# Revit family: QF_BOURGEAT_Transtherm_chariot_petit_dejeuner_6GN1_1
name_source: partatom
category: Equipement spécialisé
revit_build: Autodesk Revit 2015 (Build: 20140606_1530(x64)
units: mm (PartAtom-declared; Revit-internal decimal feet)

## types (12) — shared parameters
Charge max = 30.00 kg
Fabricant = BOURGEAT
Hauteur hors tout = 1072 mm
Longueur hors tout = 590 mm  [stored 1.9357 ft]
Profondeur hors tout = 628 mm  [stored 2.06037 ft]
Spécification du Fabricant = CHARIOT PETIT DEJEUNER ULYSSE
URL catalogue = http://www.bourgeat.fr

## per-type parameters (varying)
| type | Modèle | Poids net à vide | habillage_lateral | porte_inox | porte_transparente | support+poubelle(+788250) |
| 6GN1/1_sans_porte_sans_habillage | 788101 | 32.00 kg | Non | Non | Non | Non |
| 6GN1/1_sans_porte_avec_habillage | 788103 | 32.00 kg | Oui | Non | Non | Non |
| 6GN1/1_avec_porte_inox_sans_habillage | 788111 | 33.00 kg | Non | Oui | Non | Non |
| 6GN1/1_avec_porte_inox_avec_habillage | 788113 | 33.00 kg | Oui | Oui | Non | Non |
| 6GN1/1_avec_porte_translucide_sans_habillage | 788121 | 33.00 kg | Non | Non | Oui | Non |
| 6GN1/1_avec_porte_translucide_avec_habillage | 788123 | 33.00 kg | Oui | Non | Oui | Non |
| 6GN1/1_sans_porte_sans_habillage+poubelle | 788101+788250 | 32.00 kg | Non | Non | Non | Oui |
| 6GN1/1_avec_porte_inox_avec_habillage+poubelle | 788113+788250 | 33.00 kg | Oui | Oui | Non | Oui |
| 6GN1/1_avec_porte_inox_sans_habillage+poubelle | 788111+788250 | 33.00 kg | Non | Oui | Non | Oui |
| 6GN1/1_avec_porte_translucide_avec_habillage+poubelle | 788123+788250 | 33.00 kg | Oui | Non | Oui | Oui |
| 6GN1/1_avec_porte_translucide_sans_habillage+poubelle | 788121+788250 | 33.00 kg | Non | Non | Oui | Oui |
| 6GN1/1_sans_porte_avec_habillage+poubelle | 788103+788250 | 32.00 kg | Oui | Non | Non | Oui |

note: [stored X ft] marks values corroborated as IEEE doubles in the binary element streams (Revit-internal decimal feet)
